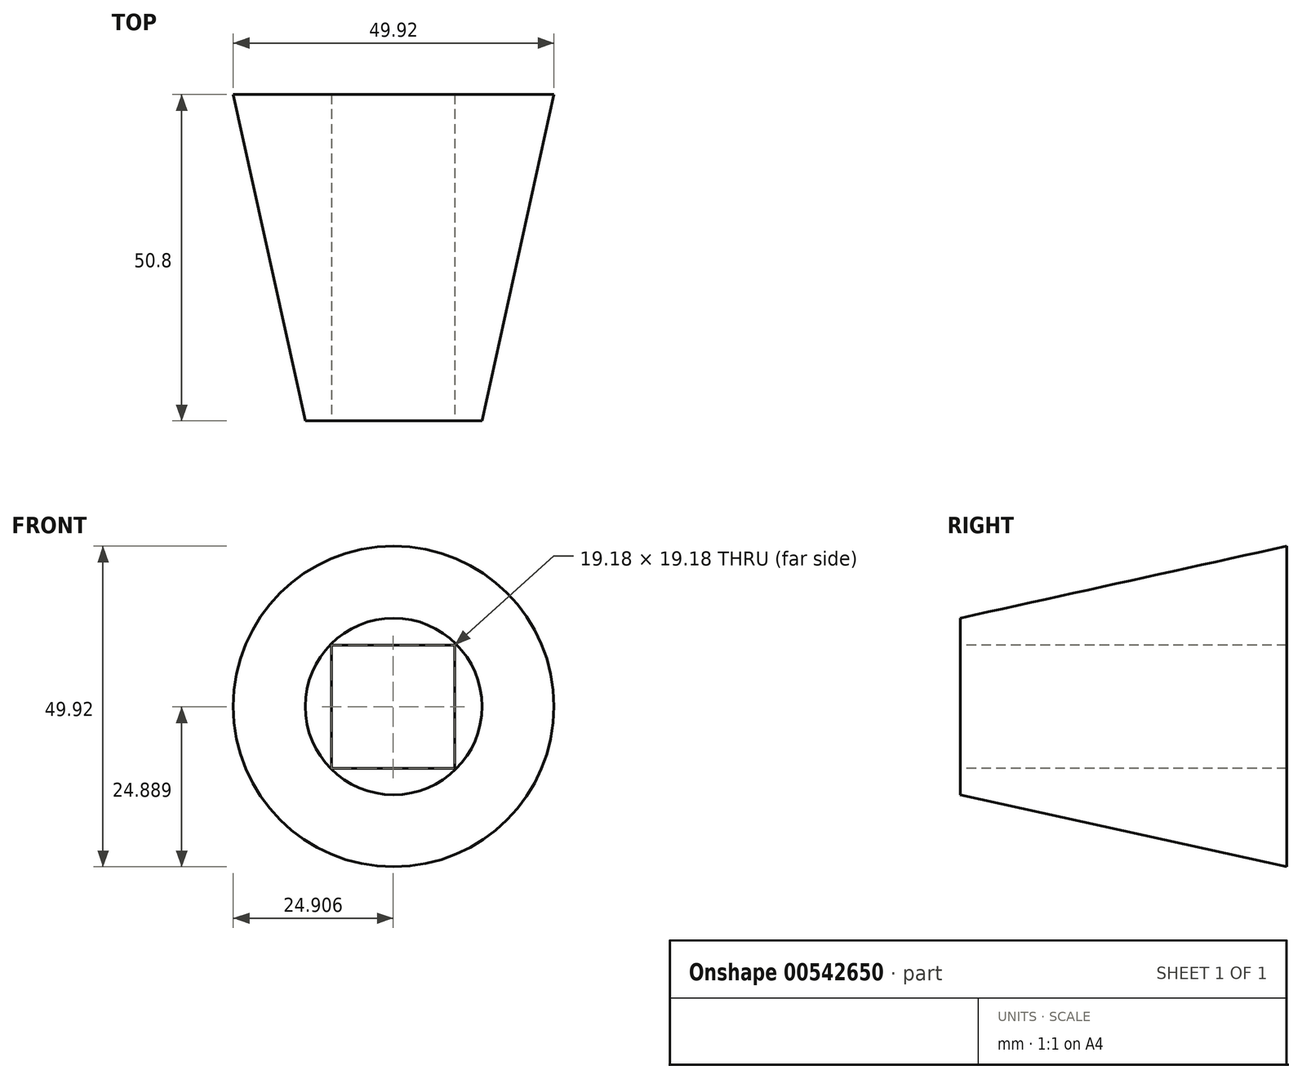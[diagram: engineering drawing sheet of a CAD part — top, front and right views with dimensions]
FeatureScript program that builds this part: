
annotation { "Feature Type Name" : "Feature", "Feature Type Description" : "" }
export const myFeature = defineFeature(function(context is Context, id is Id, definition is map)
    precondition{}
    {
        {
            var Q0;
            Q0=qCreatedBy(makeId("Front.planeOp"),FACE);
            cPlane(context, id + "F0", {"entities" : qUnion([Q0]), "cplaneType" : CPlaneType.OFFSET, "offset" : 50.8 * mm, "width" : 152.4 * mm, "height" : 152.4 * mm});
        }
        {
            var Q0;
            Q0=qCreatedBy(id+"F0.planeOp",FACE);
            var sketch = newSketch(context, id + "F1", { "sketchPlane" : qUnion([Q0])});
            skCircle(sketch, "E0", {"center": v(-0.05, -0.07) * mm, "radius": 3.18 * mm});
            skLineSegment(sketch, "E1.bottom", {"start": v(9.53, 9.52) * mm, "end": v(-9.64, 9.52) * mm});
            skLineSegment(sketch, "E1.top", {"start": v(9.53, -9.66) * mm, "end": v(-9.64, -9.66) * mm});
            skLineSegment(sketch, "E1.left", {"start": v(9.53, 9.52) * mm, "end": v(9.53, -9.66) * mm});
            skLineSegment(sketch, "E1.right", {"start": v(-9.64, 9.52) * mm, "end": v(-9.64, -9.66) * mm});
            skCircle(sketch, "E2", {"center": v(0, 0) * mm, "radius": 13.76 * mm});
            skSolve(sketch);
        }
        {
            var Q0;
            Q0=qCreatedBy(makeId("Right.planeOp"),FACE);
            var sketch = newSketch(context, id + "F2", { "sketchPlane" : qUnion([Q0])});
            skLineSegment(sketch, "E3", {"start": v(0, 0) * mm, "end": v(0, 24.96) * mm});
            skLineSegment(sketch, "E4", {"start": v(0, 24.96) * mm, "end": v(0, -24.62) * mm});
            skLineSegment(sketch, "E5", {"start": v(0, -24.62) * mm, "end": v(0, -25.4) * mm});
            skLineSegment(sketch, "E6", {"start": v(0, -25.4) * mm, "end": v(-50.8, -13.96) * mm});
            skLineSegment(sketch, "E7", {"start": v(-50.8, -13.96) * mm, "end": v(-50.8, 13.75) * mm});
            skLineSegment(sketch, "E8", {"start": v(-50.8, 13.75) * mm, "end": v(0, 24.96) * mm});
            skLineSegment(sketch, "E9", {"start": v(0, 0) * mm, "end": v(-50.8, 0) * mm});
            skLineSegment(sketch, "E10", {"start": v(-50.8, 13.75) * mm, "end": v(-50.8, -13.96) * mm});
            skSolve(sketch);
        }
        {
            var Q0;
            {var subQ0=sQuery(id+"F2.wireOp",EDGE,"E8");Q0=makeQuery(id+"F2.imprint","IMPRINT",FACE,{"disambiguationData":[TD([[makeQuery(id+"F2.imprint","IMPRINT",EDGE,{"derivedFrom":subQ0}),-1.0]])]});}
            var Q1;
            Q1=sQuery(id+"F2.wireOp",EDGE,"E9");
            revolve(context, id + "F3", {"entities" : qUnion([Q0]), "axis" : qUnion([Q1]), "revolveType" : RevolveType.FULL});
        }
        {
            var Q0;
            Q0=makeQuery(id+"F1.imprint","IMPRINT",FACE,{"disambiguationData":[TD([[makeQuery(id+"F1.imprint","IMPRINT",EDGE,{"derivedFrom":sQuery(id+"F1.wireOp",EDGE,"E0")}),-1.0]])]});
            var Q1;
            Q1=makeQuery(id+"F1.imprint","IMPRINT",FACE,{"disambiguationData":[TD([[makeQuery(id+"F1.imprint","IMPRINT",EDGE,{"derivedFrom":sQuery(id+"F1.wireOp",EDGE,"E0")}),1.0]])]});
            extrude(context, id + "F4", {"entities" : qUnion([Q0, Q1]), "operationType" : NewBodyOperationType.REMOVE, "oppositeDirection" : true, "depth" : 61.98 * mm, "offsetDistance" : 25.4 * mm});
        }
    });
